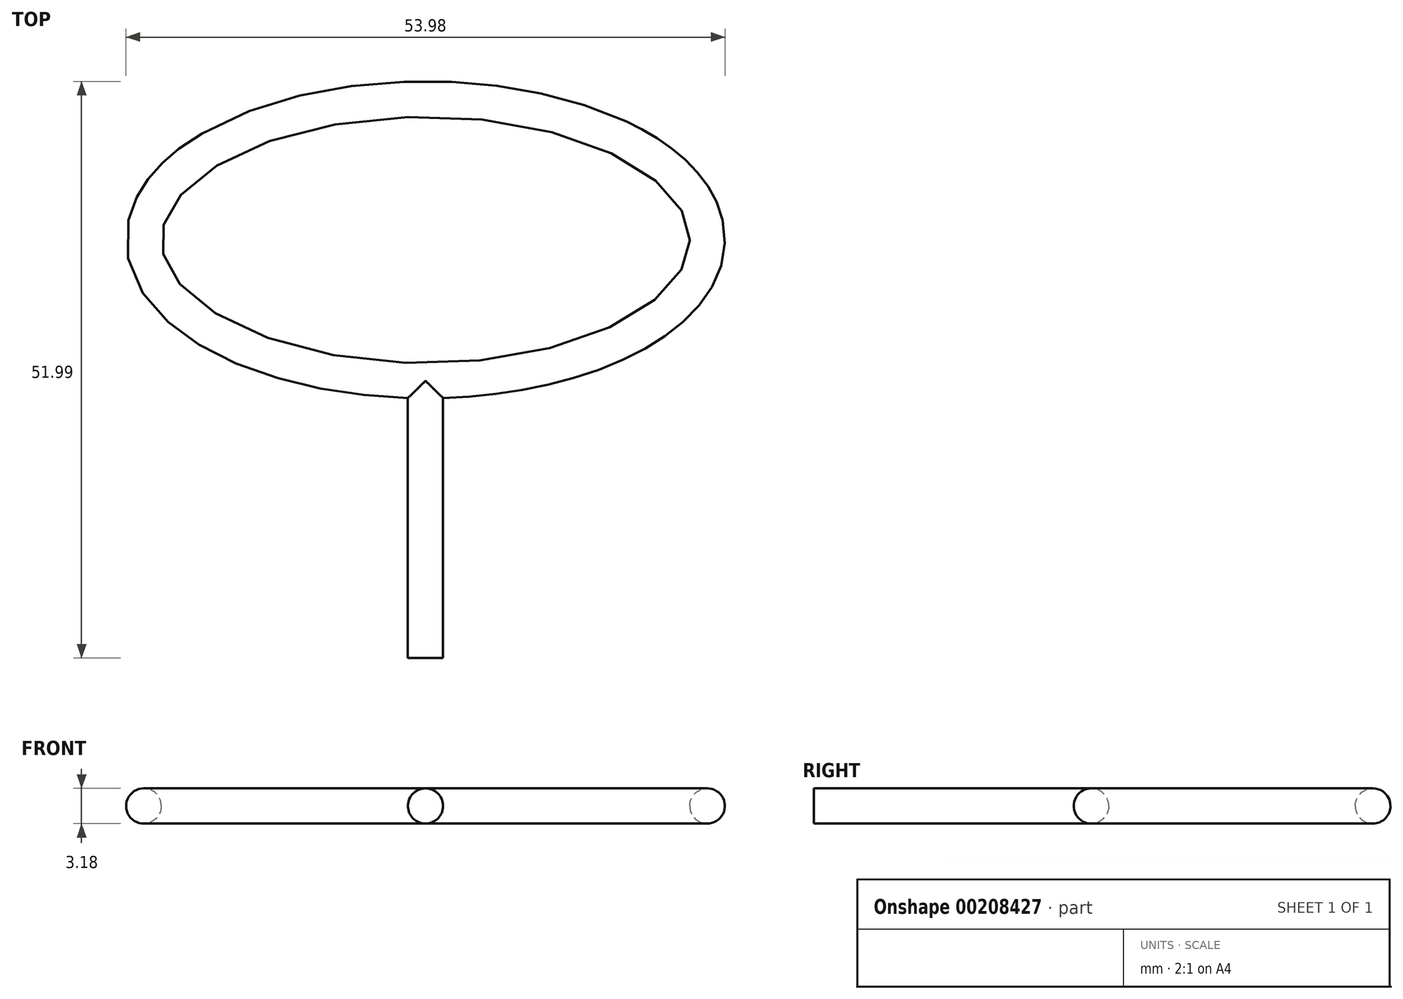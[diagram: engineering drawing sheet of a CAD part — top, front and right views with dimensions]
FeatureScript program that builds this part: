
annotation { "Feature Type Name" : "Feature", "Feature Type Description" : "" }
export const myFeature = defineFeature(function(context is Context, id is Id, definition is map)
    precondition{}
    {
        {
            var Q0;
            Q0=qCreatedBy(makeId("Top.planeOp"),FACE);
            var sketch = newSketch(context, id + "F0", { "sketchPlane" : qUnion([Q0])});
            skEllipse(sketch, "E0", {"center": v(0, 0) * mm, "majorRadius": 25.4 * mm, "minorRadius": 12.7 * mm, "majorAxis": v(-1, 0)});
            skSolve(sketch);
        }
        {
            var Q0;
            Q0=qCreatedBy(makeId("Front.planeOp"),FACE);
            var sketch = newSketch(context, id + "F1", { "sketchPlane" : qUnion([Q0])});
            skLineSegment(sketch, "E1.0", {"start": v(25.4, 0) * mm, "end": v(-25.4, 0) * mm});
            skCircle(sketch, "E2", {"center": v(-25.4, 0) * mm, "radius": 1.59 * mm});
            skSolve(sketch);
        }
        {
            var Q0;
            Q0=makeQuery(id+"F1.imprint","IMPRINT",FACE,{"disambiguationData":[TD([[makeQuery(id+"F1.imprint","IMPRINT",EDGE,{"derivedFrom":sQuery(id+"F1.wireOp",EDGE,"E2")}),1.0]])]});
            var Q1;
            Q1=sQuery(id+"F0.wireOp",EDGE,"E0");
            sweep(context, id + "F2", {"profiles" : qUnion([Q0]), "path" : qUnion([Q1])});
        }
        {
            var Q0;
            Q0=qCreatedBy(makeId("Front.planeOp"),FACE);
            cPlane(context, id + "F3", {"entities" : qUnion([Q0]), "cplaneType" : CPlaneType.OFFSET, "offset" : 12.7 * mm, "width" : 150 * mm, "height" : 150 * mm});
        }
        {
            var Q0;
            Q0=qCreatedBy(id+"F3.planeOp",FACE);
            var sketch = newSketch(context, id + "F4", { "sketchPlane" : qUnion([Q0])});
            skCircle(sketch, "E3", {"center": v(0, 0) * mm, "radius": 1.59 * mm});
            skSolve(sketch);
        }
        {
            var Q0;
            Q0 = qSketchRegion(id + "F4", true);
            extrude(context, id + "F5", {"entities" : qUnion([Q0]), "operationType" : NewBodyOperationType.ADD, "depth" : 25 * mm});
        }
    });
